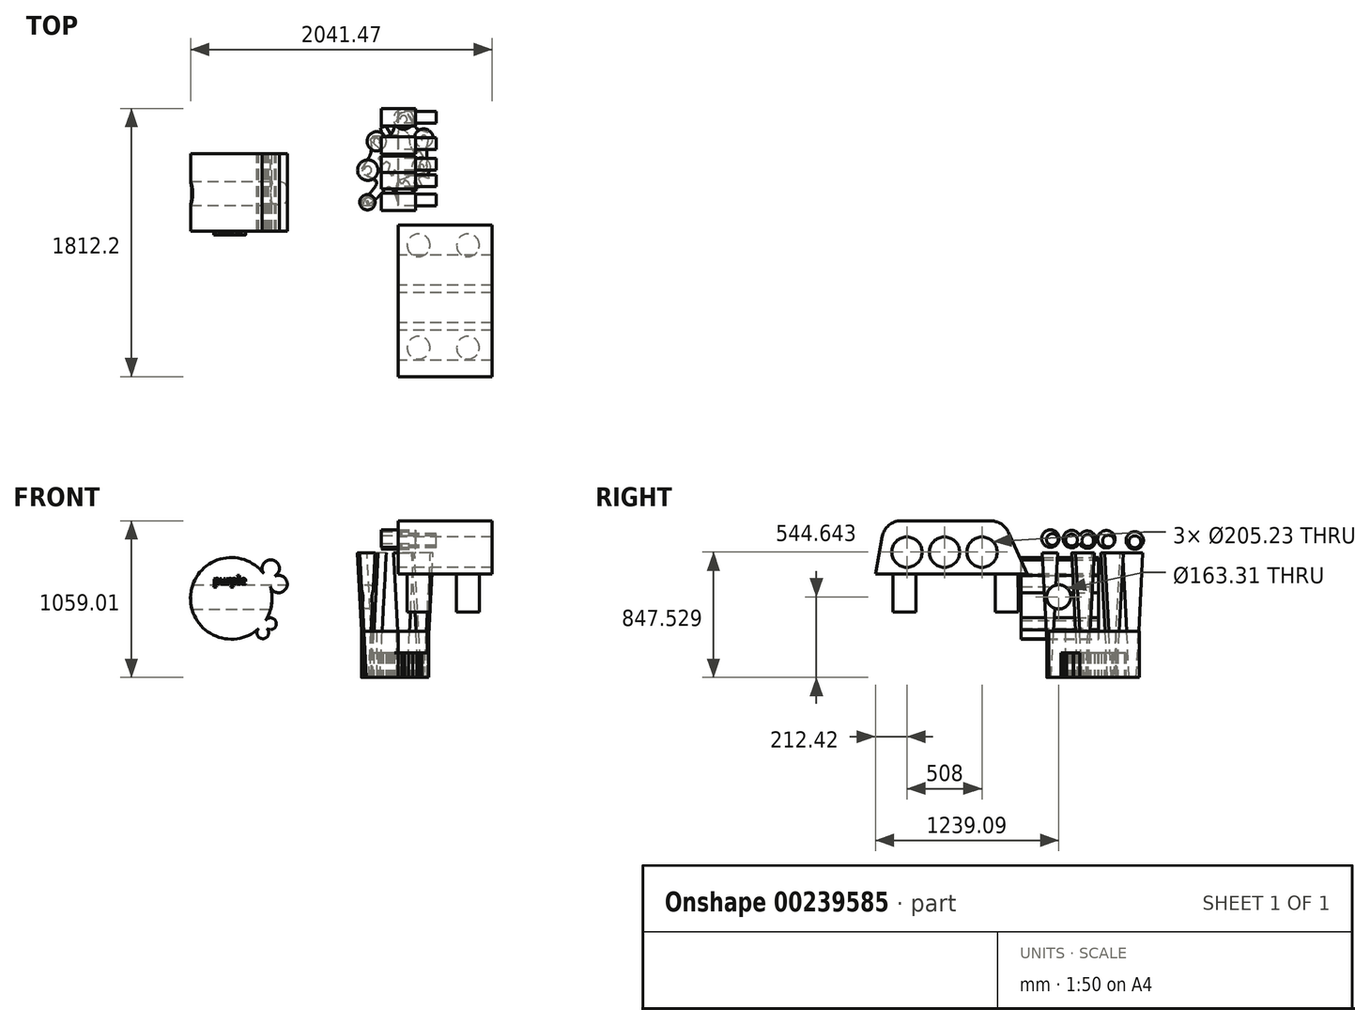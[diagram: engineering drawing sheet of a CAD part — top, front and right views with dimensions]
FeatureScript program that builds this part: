
annotation { "Feature Type Name" : "Feature", "Feature Type Description" : "" }
export const myFeature = defineFeature(function(context is Context, id is Id, definition is map)
    precondition{}
    {
        {
            var Q0;
            Q0=qCreatedBy(makeId("Top.planeOp"),FACE);
            var sketch = newSketch(context, id + "F0", { "sketchPlane" : qUnion([Q0])});
            skLineSegment(sketch, "E0", {"start": v(-190.3, 87.95) * mm, "end": v(-165.4, 120.45) * mm});
            skLineSegment(sketch, "E1", {"start": v(-165.4, 120.45) * mm, "end": v(-137.02, 98.71) * mm});
            skLineSegment(sketch, "E2", {"start": v(-137.02, 98.71) * mm, "end": v(-106.06, 115.22) * mm});
            skLineSegment(sketch, "E3", {"start": v(-106.06, 115.22) * mm, "end": v(-122.81, 173.85) * mm});
            skLineSegment(sketch, "E4", {"start": v(-122.81, 173.85) * mm, "end": v(-83.24, 185.16) * mm});
            skLineSegment(sketch, "E5", {"start": v(-83.24, 185.16) * mm, "end": v(-49.9, 124.75) * mm});
            skLineSegment(sketch, "E6", {"start": v(-49.9, 124.75) * mm, "end": v(0, 124.75) * mm});
            skLineSegment(sketch, "E7", {"start": v(0, 124.75) * mm, "end": v(9.22, 184.44) * mm});
            skLineSegment(sketch, "E8", {"start": v(9.22, 184.44) * mm, "end": v(70.42, 129.72) * mm});
            skLineSegment(sketch, "E9", {"start": v(70.42, 129.72) * mm, "end": v(80.5, 48.53) * mm});
            skLineSegment(sketch, "E10", {"start": v(80.5, 48.53) * mm, "end": v(111.53, 0) * mm});
            skLineSegment(sketch, "E11", {"start": v(111.53, 0) * mm, "end": v(140.64, 18.6) * mm});
            skLineSegment(sketch, "E12", {"start": v(140.64, 18.6) * mm, "end": v(169.35, -26.3) * mm});
            skLineSegment(sketch, "E13", {"start": v(169.35, -26.3) * mm, "end": v(146.02, -62.28) * mm});
            skLineSegment(sketch, "E14", {"start": v(146.02, -62.28) * mm, "end": v(144.29, -101.06) * mm});
            skLineSegment(sketch, "E15", {"start": v(144.29, -101.06) * mm, "end": v(198.98, -126.9) * mm});
            skLineSegment(sketch, "E16", {"start": v(198.98, -126.9) * mm, "end": v(207.02, -169.85) * mm});
            skLineSegment(sketch, "E17", {"start": v(207.02, -169.85) * mm, "end": v(157.1, -152.8) * mm});
            skLineSegment(sketch, "E18", {"start": v(157.1, -152.8) * mm, "end": v(135.68, -171.02) * mm});
            skLineSegment(sketch, "E19", {"start": v(135.68, -171.02) * mm, "end": v(157.54, -217.43) * mm});
            skLineSegment(sketch, "E20", {"start": v(157.54, -217.43) * mm, "end": v(138.49, -226.4) * mm});
            skLineSegment(sketch, "E21", {"start": v(138.49, -226.4) * mm, "end": v(118.62, -184.25) * mm});
            skLineSegment(sketch, "E22", {"start": v(118.62, -184.25) * mm, "end": v(102.93, -191.64) * mm});
            skLineSegment(sketch, "E23", {"start": v(102.93, -191.64) * mm, "end": v(126.7, -242.07) * mm});
            skLineSegment(sketch, "E24", {"start": v(126.7, -242.07) * mm, "end": v(98.82, -255.2) * mm});
            skLineSegment(sketch, "E25", {"start": v(98.82, -255.2) * mm, "end": v(70.41, -194.9) * mm});
            skLineSegment(sketch, "E26", {"start": v(70.41, -194.9) * mm, "end": v(43.83, -178.52) * mm});
            skLineSegment(sketch, "E27", {"start": v(43.83, -178.52) * mm, "end": v(25.63, -208.05) * mm});
            skLineSegment(sketch, "E28", {"start": v(25.63, -208.05) * mm, "end": v(0, -173.23) * mm});
            skLineSegment(sketch, "E29", {"start": v(0, -173.23) * mm, "end": v(0, -139.53) * mm});
            skLineSegment(sketch, "E30", {"start": v(0, -139.53) * mm, "end": v(-24.94, -110.52) * mm});
            skLineSegment(sketch, "E31", {"start": v(-24.94, -110.52) * mm, "end": v(-39.5, -154.06) * mm});
            skLineSegment(sketch, "E32", {"start": v(-39.5, -154.06) * mm, "end": v(-66.82, -118.16) * mm});
            skLineSegment(sketch, "E33", {"start": v(-66.82, -118.16) * mm, "end": v(-55.27, -76.02) * mm});
            skLineSegment(sketch, "E34", {"start": v(-55.27, -76.02) * mm, "end": v(-80.2, -55.07) * mm});
            skLineSegment(sketch, "E35", {"start": v(-80.2, -55.07) * mm, "end": v(-102.95, -74.84) * mm});
            skLineSegment(sketch, "E36", {"start": v(-102.95, -74.84) * mm, "end": v(-132.57, -28.74) * mm});
            skLineSegment(sketch, "E37", {"start": v(-132.57, -28.74) * mm, "end": v(-108.9, -6.12) * mm});
            skLineSegment(sketch, "E38", {"start": v(-108.9, -6.12) * mm, "end": v(-131.43, 37.05) * mm});
            skLineSegment(sketch, "E39", {"start": v(-131.43, 37.05) * mm, "end": v(-190.3, 87.95) * mm});
            skSolve(sketch);
        }
        {
            var Q0;
            Q0=makeQuery(id+"F0.imprint","IMPRINT",FACE,{"disambiguationData":[TD([[makeQuery(id+"F0.imprint","IMPRINT",EDGE,{"derivedFrom":sQuery(id+"F0.wireOp",EDGE,"E0")}),-1.0]])]});
            extrude(context, id + "F1", {"entities" : qUnion([Q0]), "depth" : 167.21 * mm});
        }
        {
            var Q0;
            Q0=qCreatedBy(makeId("Top.planeOp"),FACE);
            var sketch = newSketch(context, id + "F2", { "sketchPlane" : qUnion([Q0])});
            skFitSpline(sketch, "E40", {"points": [v(-193.97, -271.98) * mm, v(-235.62, -349.15) * mm, v(-131.98, -289.9) * mm, v(-53.02, -228.29) * mm, v(0, -337.6) * mm, v(0, -186.46) * mm, v(174.38, -128.88) * mm, v(192.64, 0) * mm, v(201.5, 86) * mm, v(198.64, 141.38) * mm, v(127.9, 165.87) * mm, v(69.38, 262.4) * mm, v(0, 260.25) * mm, v(-57, 122.7) * mm, v(-175.53, 111.24) * mm, v(-187.24, 0) * mm, v(-247.67, -125.44) * mm, v(-150.84, -184.81) * mm, v(-193.97, -271.98) * mm]});
            skSolve(sketch);
        }
        {
            var Q0;
            Q0 = qSketchRegion(id + "F2", true);
            extrude(context, id + "F18", {"entities" : qUnion([Q0]), "depth" : 313.03 * mm});
        }
        {
            var Q0;
            Q0=qCreatedBy(makeId("Top.planeOp"),FACE);
            var sketch = newSketch(context, id + "F19", { "sketchPlane" : qUnion([Q0])});
            skCircle(sketch, "E41", {"center": v(35.4, 231.2) * mm, "radius": 24 * mm});
            skCircle(sketch, "E42", {"center": v(172.29, 104.48) * mm, "radius": 18.24 * mm});
            skCircle(sketch, "E43", {"center": v(154.52, -92.58) * mm, "radius": 18.95 * mm});
            skCircle(sketch, "E44", {"center": v(-146.48, 82.14) * mm, "radius": 20.88 * mm});
            skCircle(sketch, "E45", {"center": v(-206.17, -112.83) * mm, "radius": 25.34 * mm});
            skCircle(sketch, "E46", {"center": v(-209.12, -329.63) * mm, "radius": 8.06 * mm});
            skSolve(sketch);
        }
        {
            var Q0;
            Q0 = qSketchRegion(id + "F19", true);
            extrude(context, id + "F3", {"entities" : qUnion([Q0]), "endBound" : BoundingType.THROUGH_ALL, "depth" : 25.4 * mm, "hasDraft" : true, "draftAngle" : 3 * degree});
        }
        {
            var Q0;
            Q0=qCreatedBy(makeId("Right.planeOp"),FACE);
            var sketch = newSketch(context, id + "F4", { "sketchPlane" : qUnion([Q0])});
            skCircle(sketch, "E47", {"center": v(-312.99, 932.9) * mm, "radius": 39.74 * mm});
            skCircle(sketch, "E48", {"center": v(-182.65, 929.34) * mm, "radius": 39.74 * mm});
            skCircle(sketch, "E49", {"center": v(-73.21, 926.35) * mm, "radius": 39.74 * mm});
            skCircle(sketch, "E50", {"center": v(66.53, 922.54) * mm, "radius": 39.74 * mm});
            skCircle(sketch, "E51", {"center": v(245.06, 917.67) * mm, "radius": 39.74 * mm});
            skLineSegment(sketch, "E52", {"start": v(493.97, 910.88) * mm, "end": v(-640.4, 941.83) * mm, "construction": true});
            skSolve(sketch);
        }
        {
            var Q0;
            Q0 = qSketchRegion(id + "F4", true);
            extrude(context, id + "F5", {"entities" : qUnion([Q0]), "depth" : 256.54 * mm});
        }
        {
            var Q0;
            Q0=qCreatedBy(makeId("Right.planeOp"),FACE);
            var sketch = newSketch(context, id + "F6", { "sketchPlane" : qUnion([Q0])});
            skCircle(sketch, "E53", {"center": v(-325.75, 939.45) * mm, "radius": 58.75 * mm});
            skCircle(sketch, "E54", {"center": v(-181.46, 936.04) * mm, "radius": 58.75 * mm});
            skCircle(sketch, "E55", {"center": v(-76.64, 932.21) * mm, "radius": 58.75 * mm});
            skCircle(sketch, "E56", {"center": v(52.68, 935.2) * mm, "radius": 58.75 * mm});
            skCircle(sketch, "E57", {"center": v(244.62, 926.68) * mm, "radius": 58.75 * mm});
            skSolve(sketch);
        }
        {
            var Q0;
            Q0 = qSketchRegion(id + "F6", true);
            extrude(context, id + "F7", {"entities" : qUnion([Q0]), "endBound" : BoundingType.SYMMETRIC, "oppositeDirection" : true, "depth" : 230.89 * mm});
        }
        {
            var Q0;
            Q0=qCreatedBy(makeId("Right.planeOp"),FACE);
            var sketch = newSketch(context, id + "F8", { "sketchPlane" : qUnion([Q0])});
            skLineSegment(sketch, "E58", {"start": v(-1367.64, 847.53) * mm, "end": v(-717.2, 847.53) * mm, "construction": true});
            skCircle(sketch, "E59", {"center": v(-1296.42, 847.53) * mm, "radius": 102.62 * mm});
            skCircle(sketch, "E60", {"center": v(-1042.42, 847.53) * mm, "radius": 102.62 * mm});
            skCircle(sketch, "E61", {"center": v(-788.42, 847.53) * mm, "radius": 102.62 * mm});
            skLineSegment(sketch, "E62", {"start": v(-1508.84, 698.22) * mm, "end": v(-1046.05, 698.22) * mm});
            skLineSegment(sketch, "E63", {"start": v(-482.68, 698.22) * mm, "end": v(-645.2, 1059) * mm});
            skLineSegment(sketch, "E64", {"start": v(-645.2, 1059) * mm, "end": v(-1443.87, 1059) * mm});
            skLineSegment(sketch, "E65", {"start": v(-1443.87, 1059) * mm, "end": v(-1508.84, 698.22) * mm});
            skPoint(sketch, "E66", {"position": v(-1042.42, 698.22) * mm});
            skLineSegment(sketch, "E67", {"start": v(-1046.05, 698.22) * mm, "end": v(-482.68, 698.22) * mm});
            skSolve(sketch);
        }
        {
            var Q0;
            Q0=makeQuery(id+"F8.imprint","IMPRINT",FACE,{"disambiguationData":[TD([[makeQuery(id+"F8.imprint","IMPRINT",EDGE,{"derivedFrom":sQuery(id+"F8.wireOp",EDGE,"E59")}),-1.0]])]});
            extrude(context, id + "F9", {"entities" : qUnion([Q0]), "depth" : 635.63 * mm});
        }
        {
            var Q0;
            Q0=makeQuery(id+"F9.opExtrude","SWEPT_EDGE",EDGE,{"disambiguationData":[OSD([sQuery(id+"F8.wireOp",EDGE,"E63"),sQuery(id+"F8.wireOp",EDGE,"E64")])]});
            var Q1;
            Q1=makeQuery(id+"F9.opExtrude","SWEPT_EDGE",EDGE,{"disambiguationData":[OSD([sQuery(id+"F8.wireOp",EDGE,"E64"),sQuery(id+"F8.wireOp",EDGE,"E65")])]});
            fillet(context, id + "F10", {"entities" : qUnion([Q0, Q1]), "radius" : 128.27 * mm, "tangentPropagation" : true, "allowEdgeOverflow" : false});
        }
        {
            var Q0;
            Q0=makeQuery(id+"F9.opExtrude","SWEPT_FACE",FACE,{"disambiguationData":[OSD([sQuery(id+"F8.wireOp",EDGE,"E62"),sQuery(id+"F8.wireOp",EDGE,"E67")])]});
            var sketch = newSketch(context, id + "F11", { "sketchPlane" : qUnion([Q0])});
            skCircle(sketch, "E68", {"center": v(137.57, 1313.26) * mm, "radius": 76.96 * mm});
            skCircle(sketch, "E69", {"center": v(471.07, 1313.26) * mm, "radius": 76.96 * mm});
            skCircle(sketch, "E70", {"center": v(137.57, 620.6) * mm, "radius": 76.96 * mm});
            skCircle(sketch, "E71", {"center": v(471.07, 620.6) * mm, "radius": 76.96 * mm});
            skSolve(sketch);
        }
        {
            var Q0;
            Q0=makeQuery(id+"F11.imprint","IMPRINT",FACE,{"disambiguationData":[TD([[makeQuery(id+"F11.imprint","IMPRINT",EDGE,{"derivedFrom":sQuery(id+"F11.wireOp",EDGE,"E68")}),1.0]])]});
            var Q1;
            Q1=makeQuery(id+"F11.imprint","IMPRINT",FACE,{"disambiguationData":[TD([[makeQuery(id+"F11.imprint","IMPRINT",EDGE,{"derivedFrom":sQuery(id+"F11.wireOp",EDGE,"E69")}),1.0]])]});
            var Q2;
            Q2=makeQuery(id+"F11.imprint","IMPRINT",FACE,{"disambiguationData":[TD([[makeQuery(id+"F11.imprint","IMPRINT",EDGE,{"derivedFrom":sQuery(id+"F11.wireOp",EDGE,"E71")}),1.0]])]});
            var Q3;
            Q3=makeQuery(id+"F11.imprint","IMPRINT",FACE,{"disambiguationData":[TD([[makeQuery(id+"F11.imprint","IMPRINT",EDGE,{"derivedFrom":sQuery(id+"F11.wireOp",EDGE,"E70")}),1.0]])]});
            extrude(context, id + "F12", {"entities" : qUnion([Q0, Q1, Q2, Q3]), "operationType" : NewBodyOperationType.ADD, "depth" : 254.25 * mm});
        }
        {
            var Q0;
            Q0=qCreatedBy(makeId("Front.planeOp"),FACE);
            var sketch = newSketch(context, id + "F13", { "sketchPlane" : qUnion([Q0])});
            skCircle(sketch, "E72", {"center": v(-1129.93, 535.06) * mm, "radius": 275.9 * mm});
            skPoint(sketch, "E72.first.point", {"position": v(-922.86, 717.38) * mm});
            skPoint(sketch, "E72.second.point", {"position": v(-1204.7, 800.64) * mm});
            skPoint(sketch, "E72.third.point", {"position": v(-875.88, 427.45) * mm});
            skCircle(sketch, "E73", {"center": v(-809.57, 631.96) * mm, "radius": 58.8 * mm});
            skPoint(sketch, "E73.first.point", {"position": v(-754.36, 611.75) * mm});
            skPoint(sketch, "E73.second.point", {"position": v(-820.6, 689.7) * mm});
            skPoint(sketch, "E73.third.point", {"position": v(-814.04, 573.34) * mm});
            skCircle(sketch, "E74", {"center": v(-862.85, 736.77) * mm, "radius": 58.8 * mm});
            skPoint(sketch, "E74.first.point", {"position": v(-860.24, 795.5) * mm});
            skPoint(sketch, "E74.second.point", {"position": v(-919.26, 753.35) * mm});
            skPoint(sketch, "E74.third.point", {"position": v(-839.16, 682.97) * mm});
            skCircle(sketch, "E75", {"center": v(-865.02, 363.14) * mm, "radius": 39.91 * mm});
            skPoint(sketch, "E75.first.point", {"position": v(-890.5, 332.42) * mm});
            skPoint(sketch, "E75.second.point", {"position": v(-888.7, 395.27) * mm});
            skPoint(sketch, "E75.third.point", {"position": v(-828.47, 347.1) * mm});
            skCircle(sketch, "E76", {"center": v(-916.59, 302.2) * mm, "radius": 39.91 * mm});
            skPoint(sketch, "E76.first.point", {"position": v(-879.5, 287.45) * mm});
            skPoint(sketch, "E76.second.point", {"position": v(-896.98, 336.97) * mm});
            skPoint(sketch, "E76.third.point", {"position": v(-956.4, 299.35) * mm});
            skSolve(sketch);
        }
        {
            var Q0;
            Q0 = qSketchRegion(id + "F13", true);
            extrude(context, id + "F20", {"entities" : qUnion([Q0]), "depth" : 524.12 * mm});
        }
        {
            var Q0;
            Q0=qCreatedBy(makeId("Right.planeOp"),FACE);
            var sketch = newSketch(context, id + "F14", { "sketchPlane" : qUnion([Q0])});
            skCircle(sketch, "E77", {"center": v(-269.75, 544.64) * mm, "radius": 81.65 * mm});
            skSolve(sketch);
        }
        {
            var Q0;
            Q0 = qSketchRegion(id + "F14", true);
            extrude(context, id + "F15", {"entities" : qUnion([Q0]), "operationType" : NewBodyOperationType.REMOVE, "oppositeDirection" : true, "depth" : 1819.08 * mm});
        }
        {
            var Q0;
            Q0=makeQuery(id+"F20.opExtrude","CAP_FACE",FACE,{"disambiguationData":[OSD([sQuery(id+"F13.wireOp",EDGE,"E72"),sQuery(id+"F13.wireOp",EDGE,"E73"),sQuery(id+"F13.wireOp",EDGE,"E74"),sQuery(id+"F13.wireOp",EDGE,"E75"),sQuery(id+"F13.wireOp",EDGE,"E76")])],"isStart":false});
            var sketch = newSketch(context, id + "F16", { "sketchPlane" : qUnion([Q0])});
            skText(sketch, "E78", { "text": "purple", "fontName": "Tinos-Regular.ttf"});
            const initialGuessF16  = {"E78": [-1.25052, 0.6293, 1, 0, 0.06258]};
            skSetInitialGuess(sketch, initialGuessF16);
            skSolve(sketch);
        }
        {
            var Q0;
            Q0 = qSketchRegion(id + "F16", true);
            extrude(context, id + "F17", {"entities" : qUnion([Q0]), "operationType" : NewBodyOperationType.ADD, "depth" : 25.4 * mm, "offsetDistance" : 25.4 * mm});
        }
    });
